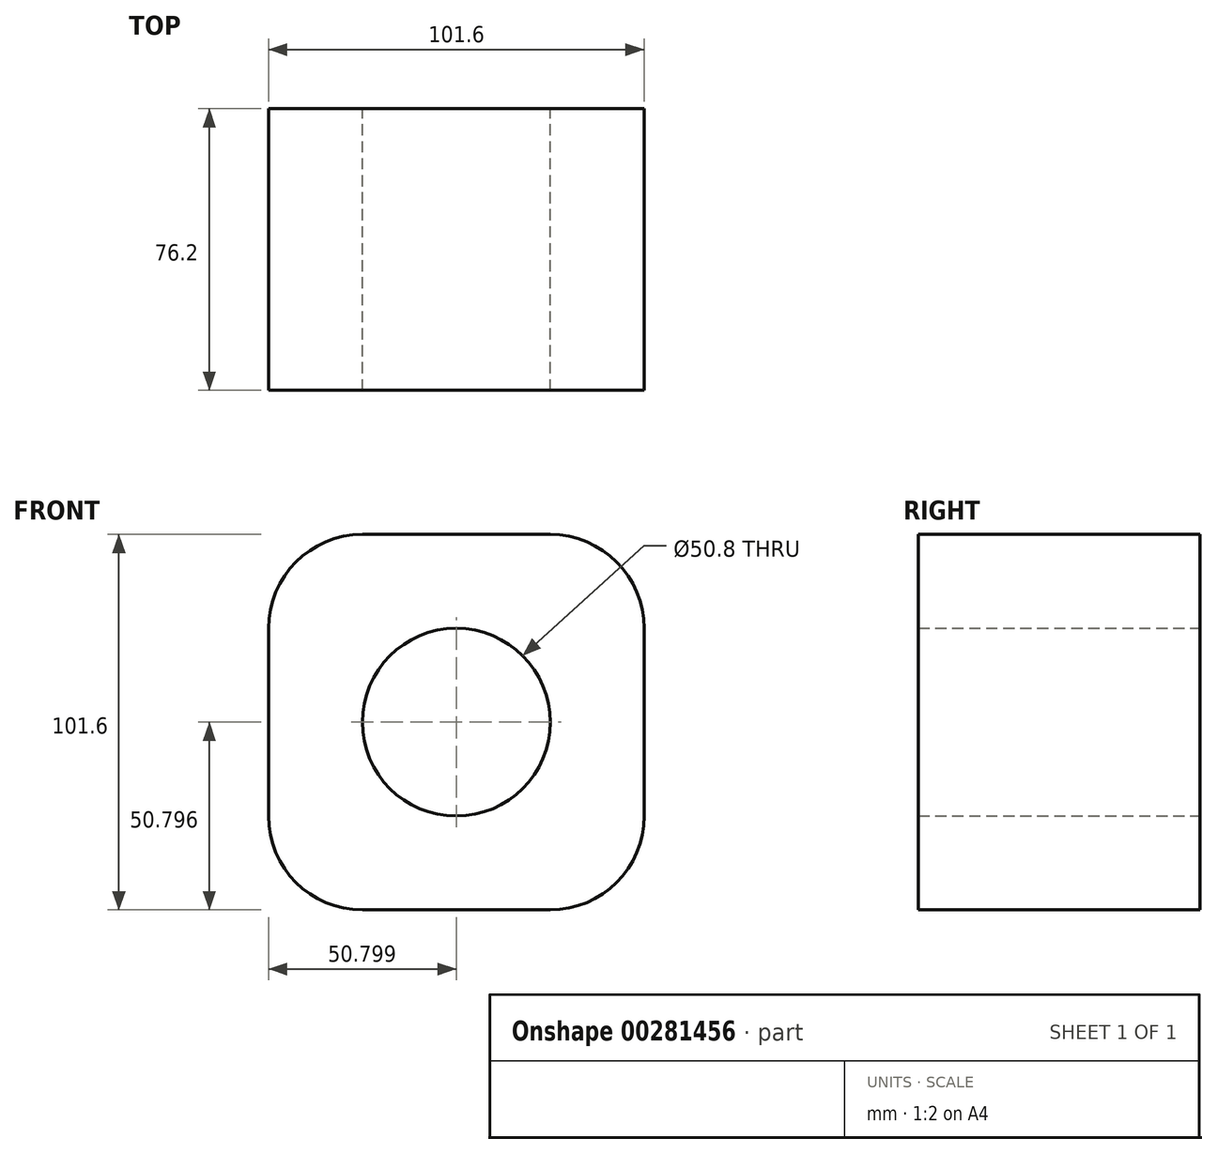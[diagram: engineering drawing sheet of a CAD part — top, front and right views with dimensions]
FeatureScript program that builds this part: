
annotation { "Feature Type Name" : "Feature", "Feature Type Description" : "" }
export const myFeature = defineFeature(function(context is Context, id is Id, definition is map)
    precondition{}
    {
        {
            var Q0;
            Q0=qCreatedBy(makeId("Front.planeOp"),FACE);
            var sketch = newSketch(context, id + "F0", { "sketchPlane" : qUnion([Q0])});
            skLineSegment(sketch, "E0.bottom", {"start": v(-30.78, 88.77) * mm, "end": v(20.02, 88.77) * mm});
            skLineSegment(sketch, "E0.top", {"start": v(-30.78, -12.83) * mm, "end": v(20.02, -12.83) * mm});
            skLineSegment(sketch, "E0.left", {"start": v(-56.18, 63.37) * mm, "end": v(-56.18, 12.57) * mm});
            skLineSegment(sketch, "E0.right", {"start": v(45.42, 63.37) * mm, "end": v(45.42, 12.57) * mm});
            skCircle(sketch, "E1", {"center": v(-5.38, 37.97) * mm, "radius": 25.4 * mm});
            skPoint(sketch, "E1.centerSnap0", {"position": v(-5.38, 88.77) * mm});
            skPoint(sketch, "E1.centerSnap1", {"position": v(-56.18, 37.97) * mm});
            skPoint(sketch, "E2.visualSharp", {"position": v(-56.18, 88.77) * mm});
            skArc(sketch, "E2.filletArc", {"start": v(-30.78, 88.77) * mm, "mid": v(-48.74, 81.33) * mm, "end": v(-56.18, 63.37) * mm});
            skPoint(sketch, "E3.visualSharp", {"position": v(45.42, 88.77) * mm});
            skArc(sketch, "E3.filletArc", {"start": v(45.42, 63.37) * mm, "mid": v(37.98, 81.33) * mm, "end": v(20.02, 88.77) * mm});
            skPoint(sketch, "E4.visualSharp", {"position": v(45.42, -12.83) * mm});
            skArc(sketch, "E4.filletArc", {"start": v(20.02, -12.83) * mm, "mid": v(37.98, -5.4) * mm, "end": v(45.42, 12.57) * mm});
            skPoint(sketch, "E5.visualSharp", {"position": v(-56.18, -12.83) * mm});
            skArc(sketch, "E5.filletArc", {"start": v(-56.18, 12.57) * mm, "mid": v(-48.74, -5.4) * mm, "end": v(-30.78, -12.83) * mm});
            skSolve(sketch);
        }
        {
            var Q0;
            Q0 = qSketchRegion(id + "F0", true);
            extrude(context, id + "F1", {"entities" : qUnion([Q0]), "depth" : 76.2 * mm});
        }
    });
